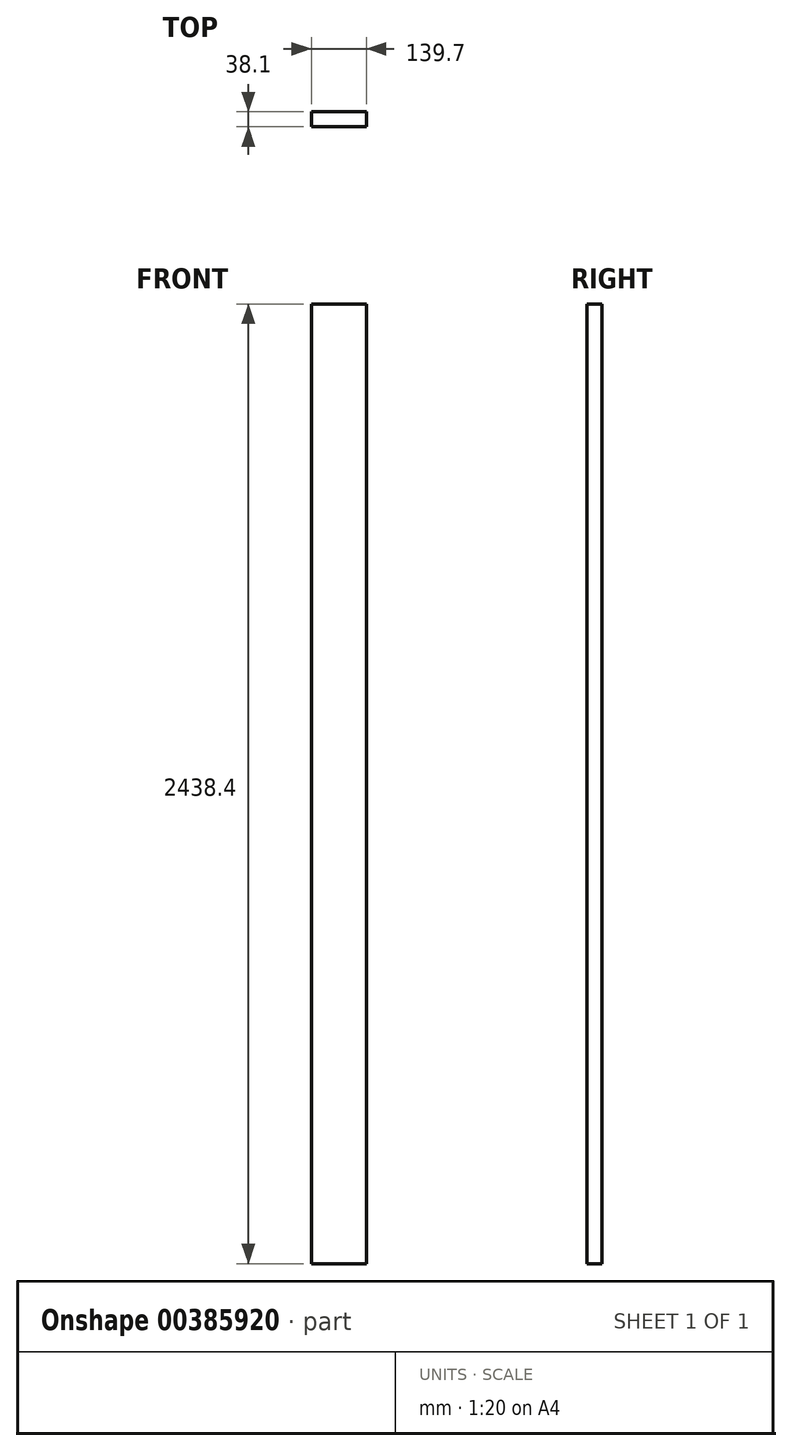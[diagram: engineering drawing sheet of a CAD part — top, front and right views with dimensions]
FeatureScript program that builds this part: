
annotation { "Feature Type Name" : "Feature", "Feature Type Description" : "" }
export const myFeature = defineFeature(function(context is Context, id is Id, definition is map)
    precondition{}
    {
        {
            var Q0;
            Q0=qCreatedBy(makeId("Top.planeOp"),FACE);
            var sketch = newSketch(context, id + "F0", { "sketchPlane" : qUnion([Q0])});
            skLineSegment(sketch, "E0.bottom", {"start": v(69.85, -19.05) * mm, "end": v(-69.85, -19.05) * mm});
            skLineSegment(sketch, "E0.top", {"start": v(69.85, 19.05) * mm, "end": v(-69.85, 19.05) * mm});
            skLineSegment(sketch, "E0.left", {"start": v(69.85, -19.05) * mm, "end": v(69.85, 19.05) * mm});
            skLineSegment(sketch, "E0.right", {"start": v(-69.85, -19.05) * mm, "end": v(-69.85, 19.05) * mm});
            skPoint(sketch, "E0.middle", {"position": v(0, 0) * mm});
            skSolve(sketch);
        }
        {
            var Q0;
            Q0 = qSketchRegion(id + "F0", true);
            extrude(context, id + "F1", {"entities" : qUnion([Q0]), "depth" : 2438.4 * mm});
        }
    });
